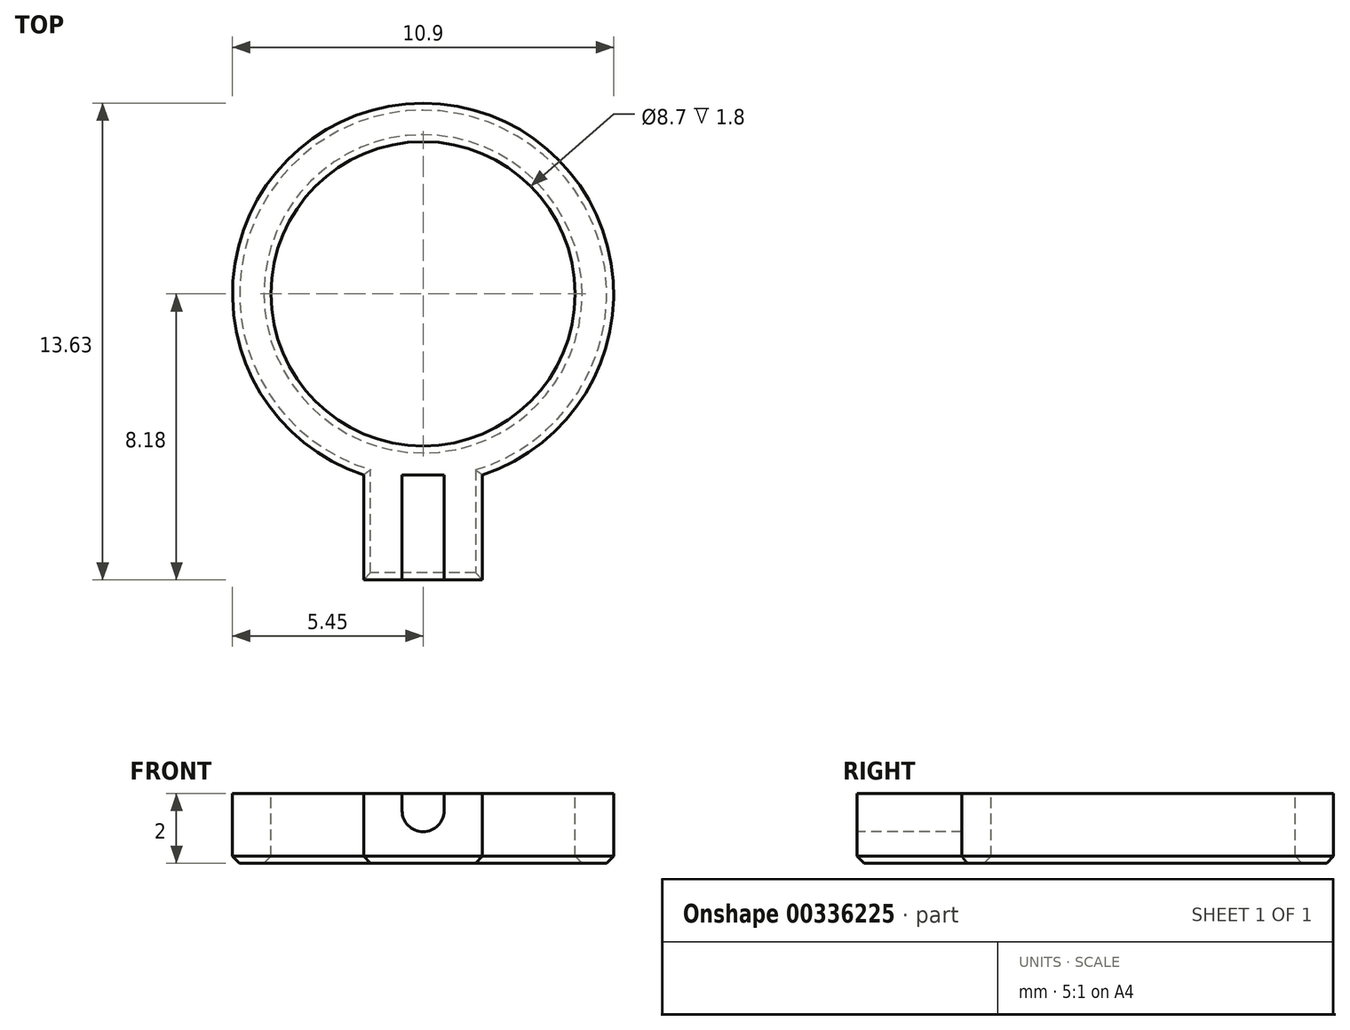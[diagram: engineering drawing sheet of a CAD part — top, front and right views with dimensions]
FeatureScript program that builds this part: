
annotation { "Feature Type Name" : "Feature", "Feature Type Description" : "" }
export const myFeature = defineFeature(function(context is Context, id is Id, definition is map)
    precondition{}
    {
        {
            var Q0;
            Q0=qCreatedBy(makeId("Top.planeOp"),FACE);
            var sketch = newSketch(context, id + "F0", { "sketchPlane" : qUnion([Q0])});
            skCircle(sketch, "E0", {"center": v(0, 0) * mm, "radius": 4.25 * mm, "construction": true});
            skArc(sketch, "E1.0", {"start": v(1.7, -5.18) * mm, "mid": v(0, 5.45) * mm, "end": v(-1.7, -5.18) * mm});
            skCircle(sketch, "E2.0", {"center": v(0, 0) * mm, "radius": 4.35 * mm});
            skLineSegment(sketch, "E3", {"start": v(-1.7, -5.18) * mm, "end": v(-1.7, -8.18) * mm});
            skLineSegment(sketch, "E4", {"start": v(-1.7, -8.18) * mm, "end": v(1.7, -8.18) * mm});
            skLineSegment(sketch, "E5", {"start": v(1.7, -8.18) * mm, "end": v(1.7, -5.18) * mm});
            skSolve(sketch);
        }
        {
            var Q0;
            Q0=qCreatedBy(makeId("Front.planeOp"),FACE);
            var sketch = newSketch(context, id + "F1", { "sketchPlane" : qUnion([Q0])});
            skLineSegment(sketch, "E6", {"start": v(0, 0) * mm, "end": v(0, 2) * mm});
            skSolve(sketch);
        }
        {
            var Q0;
            Q0 = qSketchRegion(id + "F0", true);
            var Q1;
            Q1=sQuery(id+"F1.wireOp",EDGE,"E6");
            sweep(context, id + "F2", {"profiles" : qUnion([Q0]), "path" : qUnion([Q1])});
        }
        {
            var Q0;
            Q0=makeQuery(id+"F2.opSweep","SWEPT_FACE",FACE,{"disambiguationData":[OSD([sQuery(id+"F0.wireOp",EDGE,"E4"),sQuery(id+"F1.wireOp",EDGE,"E6")])]});
            var sketch = newSketch(context, id + "F3", { "sketchPlane" : qUnion([Q0])});
            skLineSegment(sketch, "E7", {"start": v(0, 0) * mm, "end": v(0, 1.5) * mm, "construction": true});
            skPoint(sketch, "E7.endSnap0", {"position": v(0, 0) * mm});
            skCircle(sketch, "E8", {"center": v(0, 1.5) * mm, "radius": 0.5 * mm, "construction": true});
            skArc(sketch, "E9.0", {"start": v(-0.6, 1.5) * mm, "mid": v(0, 0.9) * mm, "end": v(0.6, 1.5) * mm});
            skLineSegment(sketch, "E10", {"start": v(-0.6, 1.5) * mm, "end": v(-0.6, 2) * mm});
            skLineSegment(sketch, "E11", {"start": v(0.6, 1.5) * mm, "end": v(0.6, 2) * mm});
            skLineSegment(sketch, "E12", {"start": v(0.6, 2) * mm, "end": v(-0.6, 2) * mm});
            skSolve(sketch);
        }
        {
            var Q0;
            Q0 = qSketchRegion(id + "F3", true);
            extrude(context, id + "F4", {"entities" : qUnion([Q0]), "operationType" : NewBodyOperationType.REMOVE, "oppositeDirection" : true, "depth" : 3 * mm});
        }
        {
            var Q0;
            Q0=makeQuery(id+"F2.opSweep","CAP_FACE",FACE,{"disambiguationData":[OSD([sQuery(id+"F0.wireOp",EDGE,"E1.0"),sQuery(id+"F0.wireOp",EDGE,"E2.0"),sQuery(id+"F0.wireOp",EDGE,"E3"),sQuery(id+"F0.wireOp",EDGE,"E4"),sQuery(id+"F0.wireOp",EDGE,"E5"),sQuery(id+"F1.wireOp",VERTEX,"E6.start")])],"isStart":true});
            chamfer(context, id + "F5", {"entities" : qUnion([Q0]), "width" : 0.2 * mm});
        }
    });
